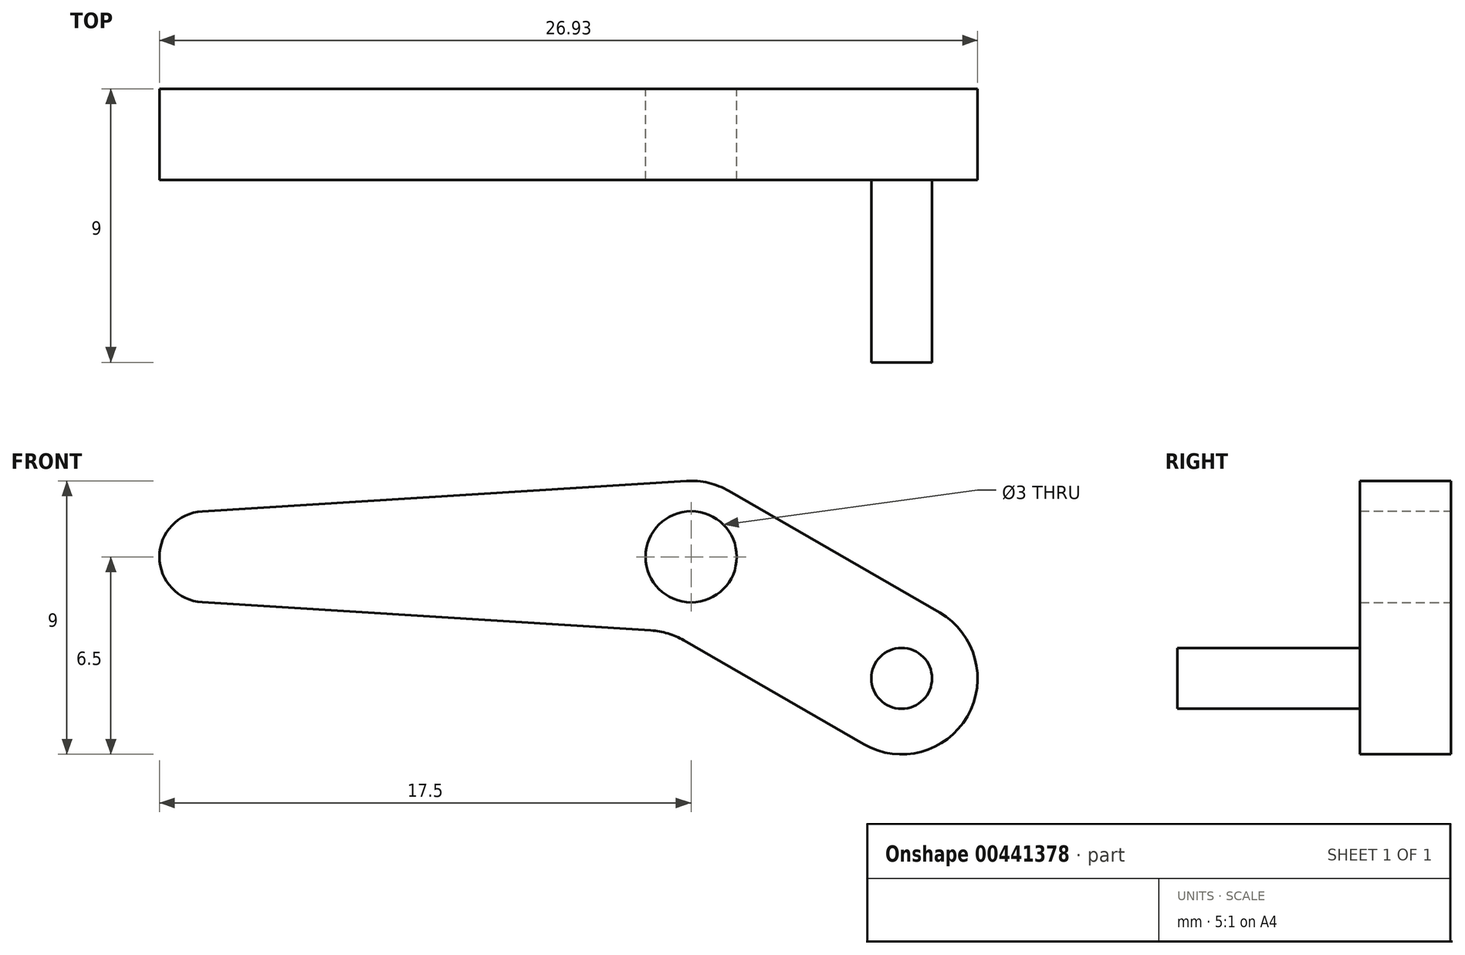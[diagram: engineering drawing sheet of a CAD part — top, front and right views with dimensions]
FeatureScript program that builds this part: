
annotation { "Feature Type Name" : "Feature", "Feature Type Description" : "" }
export const myFeature = defineFeature(function(context is Context, id is Id, definition is map)
    precondition{}
    {
        {
            var Q0;
            Q0=qCreatedBy(makeId("Front.planeOp"),FACE);
            var sketch = newSketch(context, id + "F0", { "sketchPlane" : qUnion([Q0])});
            skArc(sketch, "E0", {"start": v(1.25, 2.17) * mm, "mid": v(0.57, 2.43) * mm, "end": v(-0.16, 2.5) * mm});
            skArc(sketch, "E1", {"start": v(-16.1, 1.5) * mm, "mid": v(-17.5, 0) * mm, "end": v(-16.1, -1.5) * mm});
            skLineSegment(sketch, "E2", {"start": v(-16.1, 1.5) * mm, "end": v(-0.16, 2.5) * mm});
            skPoint(sketch, "E3.orphan", {"position": v(-40, 0) * mm});
            skLineSegment(sketch, "E4", {"start": v(-16.1, -1.5) * mm, "end": v(-1.33, -2.42) * mm});
            skCircle(sketch, "E5", {"center": v(0, 0) * mm, "radius": 1.5 * mm});
            skLineSegment(sketch, "E6", {"start": v(1.25, 2.17) * mm, "end": v(8.18, -1.83) * mm});
            skLineSegment(sketch, "E7", {"start": v(-0.23, -2.75) * mm, "end": v(5.68, -6.17) * mm});
            skArc(sketch, "E8", {"start": v(5.68, -6.17) * mm, "mid": v(9.1, -5.25) * mm, "end": v(8.18, -1.83) * mm});
            skPoint(sketch, "E9.visualSharp", {"position": v(-0.74, -2.46) * mm});
            skArc(sketch, "E9.filletArc", {"start": v(-0.23, -2.75) * mm, "mid": v(-0.76, -2.52) * mm, "end": v(-1.33, -2.42) * mm});
            skSolve(sketch);
        }
        {
            var Q0;
            Q0 = qSketchRegion(id + "F0", true);
            extrude(context, id + "F1", {"entities" : qUnion([Q0]), "depth" : 3 * mm});
        }
        {
            var Q0;
            Q0=makeQuery(id+"F1.opExtrude","CAP_FACE",FACE,{"disambiguationData":[OSD([sQuery(id+"F0.wireOp",EDGE,"E0"),sQuery(id+"F0.wireOp",EDGE,"E1"),sQuery(id+"F0.wireOp",EDGE,"E2"),sQuery(id+"F0.wireOp",EDGE,"E4"),sQuery(id+"F0.wireOp",EDGE,"E5"),sQuery(id+"F0.wireOp",EDGE,"E6"),sQuery(id+"F0.wireOp",EDGE,"E7"),sQuery(id+"F0.wireOp",EDGE,"E8"),sQuery(id+"F0.wireOp",EDGE,"E9.filletArc")])],"isStart":false});
            var sketch = newSketch(context, id + "F2", { "sketchPlane" : qUnion([Q0])});
            skCircle(sketch, "E10", {"center": v(6.93, -4) * mm, "radius": 1 * mm});
            skSolve(sketch);
        }
        {
            var Q0;
            Q0 = qSketchRegion(id + "F2", true);
            extrude(context, id + "F3", {"entities" : qUnion([Q0]), "operationType" : NewBodyOperationType.ADD, "depth" : 6 * mm});
        }
    });
